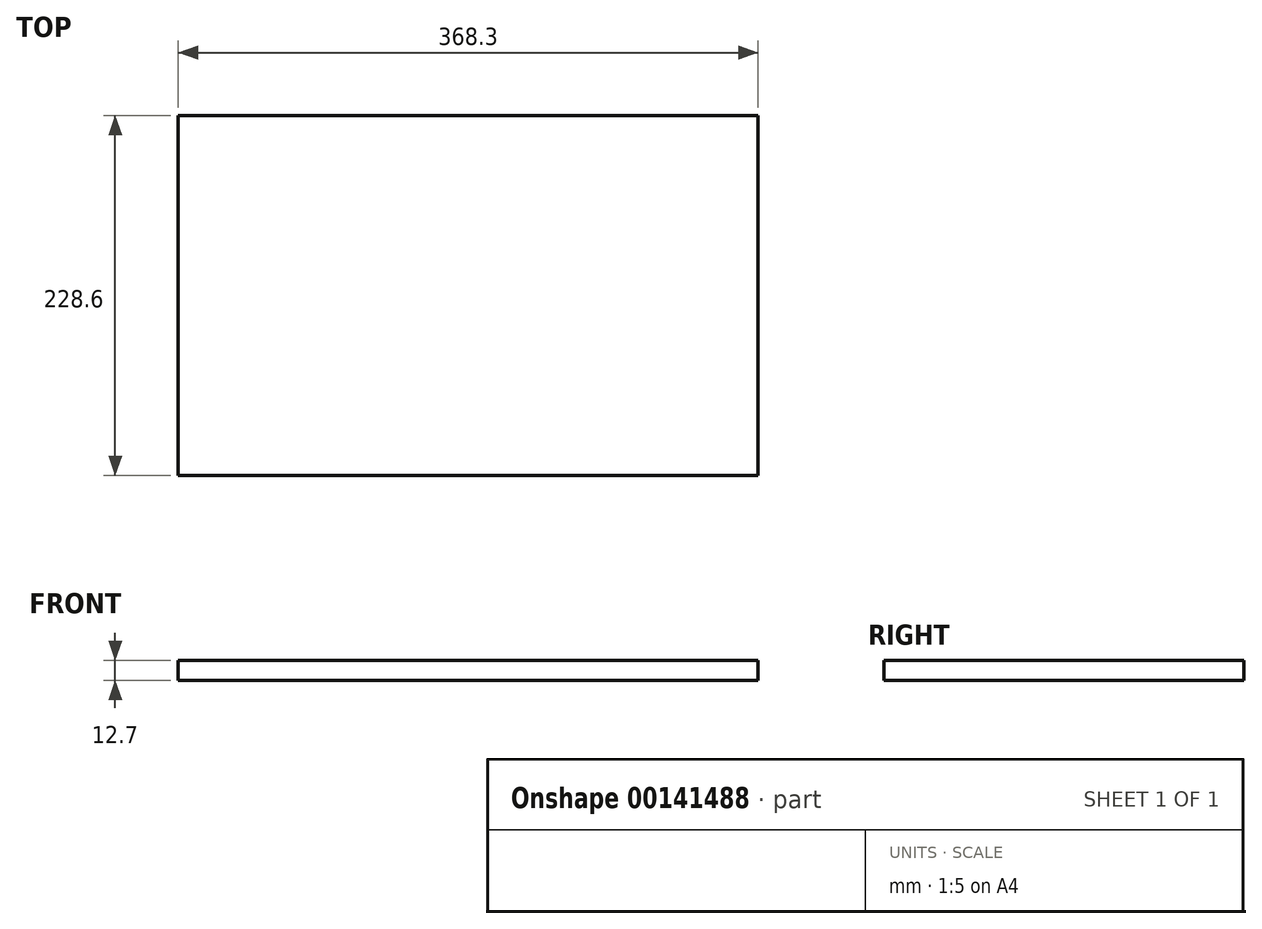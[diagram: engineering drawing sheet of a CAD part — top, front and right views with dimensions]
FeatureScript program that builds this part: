
annotation { "Feature Type Name" : "Feature", "Feature Type Description" : "" }
export const myFeature = defineFeature(function(context is Context, id is Id, definition is map)
    precondition{}
    {
        {
            var Q0;
            Q0=qCreatedBy(makeId("Top.planeOp"),FACE);
            var sketch = newSketch(context, id + "F0", { "sketchPlane" : qUnion([Q0])});
            skLineSegment(sketch, "E0.bottom", {"start": v(-184.15, 114.3) * mm, "end": v(184.15, 114.3) * mm});
            skLineSegment(sketch, "E0.top", {"start": v(-184.15, -114.3) * mm, "end": v(184.15, -114.3) * mm});
            skLineSegment(sketch, "E0.left", {"start": v(-184.15, 114.3) * mm, "end": v(-184.15, -114.3) * mm});
            skLineSegment(sketch, "E0.right", {"start": v(184.15, 114.3) * mm, "end": v(184.15, -114.3) * mm});
            skLineSegment(sketch, "E1", {"start": v(-184.15, -114.3) * mm, "end": v(184.15, 114.3) * mm, "construction": true});
            skSolve(sketch);
        }
        {
            var Q0;
            Q0=makeQuery(id+"F0.imprint","IMPRINT",FACE,{"disambiguationData":[TD([[makeQuery(id+"F0.imprint","IMPRINT",EDGE,{"derivedFrom":sQuery(id+"F0.wireOp",EDGE,"E0.bottom")}),-1.0]])]});
            extrude(context, id + "F1", {"entities" : qUnion([Q0]), "depth" : 12.7 * mm});
        }
    });
